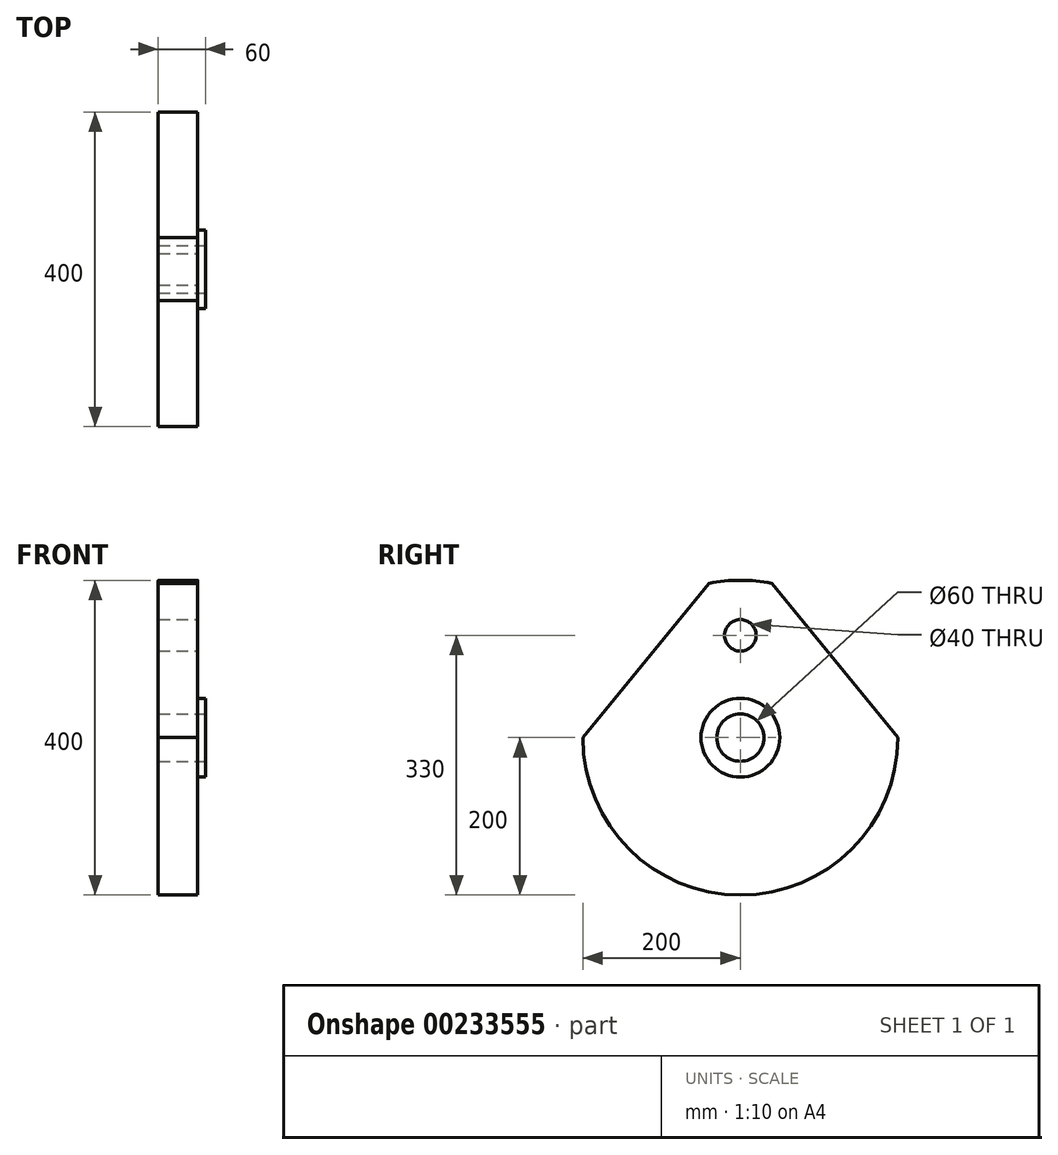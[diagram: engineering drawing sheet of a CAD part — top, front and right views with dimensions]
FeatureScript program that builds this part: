
annotation { "Feature Type Name" : "Feature", "Feature Type Description" : "" }
export const myFeature = defineFeature(function(context is Context, id is Id, definition is map)
    precondition{}
    {
        {
            var Q0;
            Q0=qCreatedBy(makeId("Right.planeOp"),FACE);
            var sketch = newSketch(context, id + "F0", { "sketchPlane" : qUnion([Q0])});
            skArc(sketch, "E0", {"start": v(-200, 0) * mm, "mid": v(0, -200) * mm, "end": v(200, 0) * mm});
            skCircle(sketch, "E1", {"center": v(0, 0) * mm, "radius": 50 * mm});
            skCircle(sketch, "E2", {"center": v(0, 0) * mm, "radius": 30 * mm, "construction": true});
            skLineSegment(sketch, "E3", {"start": v(-200, 0) * mm, "end": v(-40, 195.96) * mm});
            skLineSegment(sketch, "E4", {"start": v(0, -200) * mm, "end": v(0, 200) * mm, "construction": true});
            skLineSegment(sketch, "E5.MirrorCS", {"start": v(200, 0) * mm, "end": v(40, 195.96) * mm});
            skArc(sketch, "E6.trimOffspring", {"start": v(40, 195.96) * mm, "mid": v(0, 200) * mm, "end": v(-40, 195.96) * mm});
            skCircle(sketch, "E7", {"center": v(0, 130) * mm, "radius": 20 * mm, "construction": true});
            skSolve(sketch);
        }
        {
            var Q0;
            Q0=makeQuery(id+"F0.imprint","IMPRINT",FACE,{"disambiguationData":[TD([[makeQuery(id+"F0.imprint","IMPRINT",EDGE,{"derivedFrom":sQuery(id+"F0.wireOp",EDGE,"E0")}),1.0]])]});
            var Q1;
            Q1=makeQuery(id+"F0.imprint","IMPRINT",FACE,{"disambiguationData":[TD([[makeQuery(id+"F0.imprint","IMPRINT",EDGE,{"derivedFrom":sQuery(id+"F0.wireOp",EDGE,"E1")}),1.0]])]});
            extrude(context, id + "F1", {"entities" : qUnion([Q0, Q1]), "oppositeDirection" : true, "depth" : 50 * mm});
        }
        {
            var Q0;
            Q0=makeQuery(id+"F0.imprint","IMPRINT",FACE,{"disambiguationData":[TD([[makeQuery(id+"F0.imprint","IMPRINT",EDGE,{"derivedFrom":sQuery(id+"F0.wireOp",EDGE,"E1")}),1.0]])]});
            extrude(context, id + "F2", {"entities" : qUnion([Q0]), "operationType" : NewBodyOperationType.ADD, "depth" : 10 * mm});
        }
        {
            var Q0;
            Q0=makeQuery(id+"F2.opExtrude","CAP_FACE",FACE,{"disambiguationData":[OSD([sQuery(id+"F0.wireOp",EDGE,"E1")])],"isStart":false});
            var sketch = newSketch(context, id + "F3", { "sketchPlane" : qUnion([Q0])});
            skCircle(sketch, "E8.0", {"center": v(0, 0) * mm, "radius": 30 * mm, "construction": true});
            skSolve(sketch);
        }
        {
            var Q0;
            Q0=sQuery(id+"F3.wireOp",VERTEX,"E8.0.center");
            var Q1;
            Q1=makeQuery(id+"F1.opExtrude","SWEPT_BODY",BODY,{"disambiguationData":[OSD([sQuery(id+"F0.wireOp",EDGE,"E0"),sQuery(id+"F0.wireOp",EDGE,"E3"),sQuery(id+"F0.wireOp",EDGE,"E5.MirrorCS"),sQuery(id+"F0.wireOp",EDGE,"E6.trimOffspring")])]});
            hole(context, id + "F4", {"style" : HoleStyle.SIMPLE, "endStyle" : HoleEndStyle.THROUGH, "holeDiameter" : 60 * mm, "startFromSketch" : true, "locations" : qUnion([Q0]), "scope" : qUnion([Q1]), "isTappedThrough" : true});
        }
        {
            var Q0;
            Q0=sQuery(id+"F0.wireOp",VERTEX,"E7.center");
            var Q1;
            Q1=makeQuery(id+"F1.opExtrude","SWEPT_BODY",BODY,{"disambiguationData":[OSD([sQuery(id+"F0.wireOp",EDGE,"E0"),sQuery(id+"F0.wireOp",EDGE,"E3"),sQuery(id+"F0.wireOp",EDGE,"E5.MirrorCS"),sQuery(id+"F0.wireOp",EDGE,"E6.trimOffspring")])]});
            hole(context, id + "F5", {"style" : HoleStyle.SIMPLE, "endStyle" : HoleEndStyle.THROUGH, "holeDiameter" : 40 * mm, "startFromSketch" : true, "locations" : qUnion([Q0]), "scope" : qUnion([Q1]), "isTappedThrough" : true});
        }
    });
